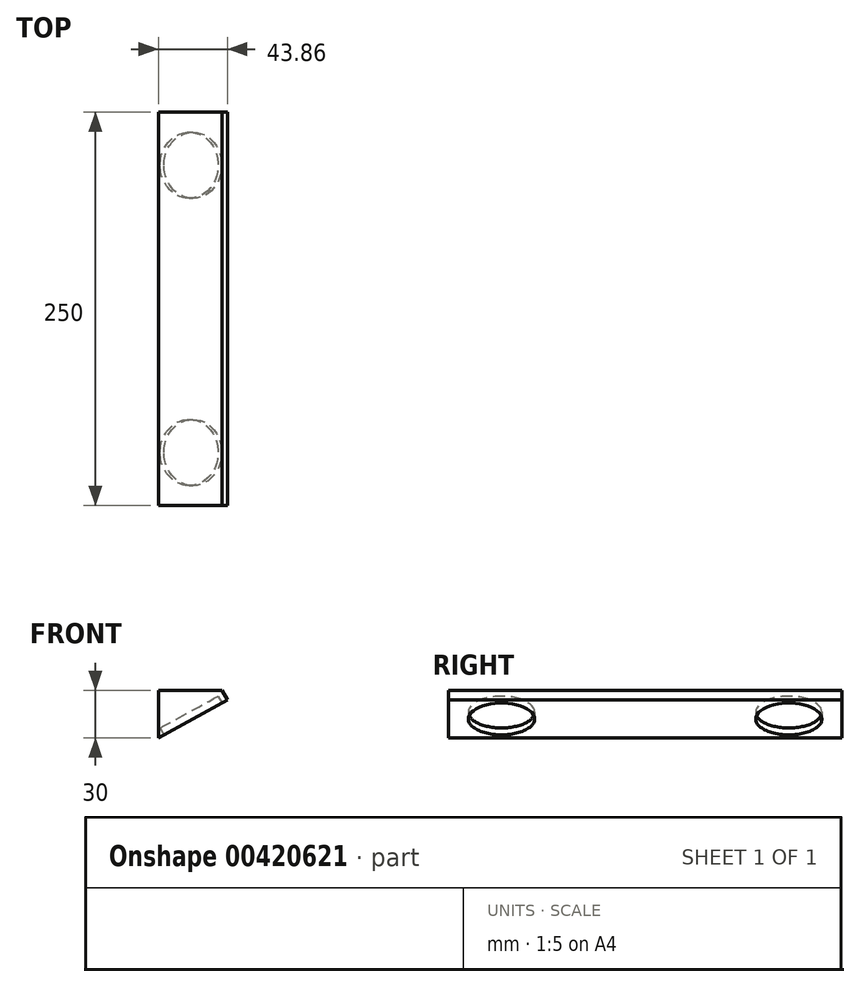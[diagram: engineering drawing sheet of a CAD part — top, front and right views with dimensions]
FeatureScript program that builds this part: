
annotation { "Feature Type Name" : "Feature", "Feature Type Description" : "" }
export const myFeature = defineFeature(function(context is Context, id is Id, definition is map)
    precondition{}
    {
        {
            var Q0;
            Q0=qCreatedBy(makeId("Front.planeOp"),FACE);
            var sketch = newSketch(context, id + "F0", { "sketchPlane" : qUnion([Q0])});
            skLineSegment(sketch, "E0", {"start": v(0, 0) * mm, "end": v(0, 30) * mm});
            skLineSegment(sketch, "E1", {"start": v(0, 30) * mm, "end": v(40.58, 30) * mm});
            skLineSegment(sketch, "E2", {"start": v(40.58, 30) * mm, "end": v(43.86, 24.01) * mm});
            skLineSegment(sketch, "E3", {"start": v(43.86, 24.01) * mm, "end": v(0, 0) * mm});
            skLineSegment(sketch, "E4", {"start": v(21.93, 12) * mm, "end": v(43.86, -28.05) * mm, "construction": true});
            skLineSegment(sketch, "E5", {"start": v(43.86, -28.05) * mm, "end": v(43.86, 24.01) * mm, "construction": true});
            skSolve(sketch);
        }
        {
            var Q0;
            Q0 = qSketchRegion(id + "F0", true);
            extrude(context, id + "F1", {"entities" : qUnion([Q0]), "depth" : 250 * mm, "symmetric" : true});
        }
        {
            var Q0;
            Q0=makeQuery(id+"F1.opExtrude","SWEPT_FACE",FACE,{"disambiguationData":[OSD([sQuery(id+"F0.wireOp",EDGE,"E3")])]});
            var sketch = newSketch(context, id + "F2", { "sketchPlane" : qUnion([Q0])});
            skCircle(sketch, "E6", {"center": v(25, 91.25) * mm, "radius": 21 * mm});
            skCircle(sketch, "E7", {"center": v(25, -91.25) * mm, "radius": 21 * mm});
            skLineSegment(sketch, "E8", {"start": v(25, 91.25) * mm, "end": v(25, -91.25) * mm, "construction": true});
            skLineSegment(sketch, "E9", {"start": v(25, 0) * mm, "end": v(0, 0) * mm, "construction": true});
            skSolve(sketch);
        }
        {
            var Q0;
            Q0 = qSketchRegion(id + "F2", true);
            extrude(context, id + "F3", {"entities" : qUnion([Q0]), "operationType" : NewBodyOperationType.REMOVE, "oppositeDirection" : true, "depth" : 5 * mm});
        }
    });
